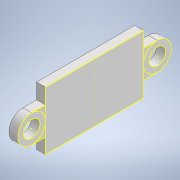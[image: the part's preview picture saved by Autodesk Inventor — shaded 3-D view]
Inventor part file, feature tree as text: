
AUTODESK INVENTOR PART (.ipt)
format: ipt  version: 2022 (Build 260153070, 153G)  size: 120,832 bytes
history: native  units: in
note: dims shown in document units (in); Inventor stores cm internally (conversion verified against a paired STEP export)
features: other x3, sketch x1
ambient origin geometry x8: Origin, YZ Plane, XZ Plane, XY Plane, X Axis, Y Axis, Z Axis, Center Point
bodies: Solid1 (feature_tree)
feature tree (4):
  other  "VL53L1X board.ipt"
  other  "Solid1::VL53L1X board.ipt"
  other  "TaggingFeature1"
  sketch  "Sketch1"  dims[d0=0.3937in]
